# Revit family: LJT-CM
name_source: partatom
category: Lighting Fixtures
revit_build: Autodesk Revit 2013 (Build: 20130531_2115(x64)
units: mm (PartAtom-declared; Revit-internal decimal feet)

## types (8) — shared parameters
Cable Height = 24"
Ceiling Type = Cable Mount
Color Filter = 16777215
Default Elevation = 48"
Description = LED Troffer with Advanced Solid State Technology
Dimming Lamp Color Temperature Shift = Incandescent Lamp Curve
Door = White Flush Steel
Emit Shape Visible in Rendering = No
Finish = Hubbell-Arctic White
Lamp = LED
Load Classification = Lighting
Manufacturer = Columbia Lighting
Manufacturer Fax = 866-898-1065
Model = LJT-CM
Photometric Notes = More IES files download Photometric Web Link
Photometric Web Link = http://www.columbialighting.com
Power Factor = 1
Product Documentation Link = http://cdn.columbialighting.com
Product Page URL = http://www.columbialighting.com
Shielding = Pattern 12 Acrylic Lens
Tilt Angle = 90.00°
URL = http://www.columbialighting.com
Voltage = 120 V

## per-type parameters (varying)
| type | Apparent Load | Color Temp | Emit from Rectangle Length | Emit from Rectangle Width | Glass | Lumen Output | Photometric Web File | Size Option | Wattage Comments | Watts | zz Width 1 |
| LJT24-50XLCM-FSA12-EU | 73 VA | 5000K | 47" | 23" | Hubbell - White Glass | Extra High Lumen | LJT24-50XLG-FSA12-EU.ies | LJT : 24 | 73W | 73 W | 48" |
| LJT24-40XWCM-FSA12-EU | 20 VA | 4000K | 47" | 23" | Hubbell - White Glass | Extra Low Lumen | LJT24-40XWG-FSA12-EU.ies | LJT : 24 | 20W | 20 W | 48" |
| LJT22-50VWCM-FSA12-EU | 13 VA | 5000K | 23" | 23" | Hubbell - White Glass | Very High Lumen | LJT22-50VWG-FSA12-EU.ies | LJT : 22 | 13W | 13 W | 24" |
| LJT14-30MWCM-FSA12-EU | 31 VA | 3000K | 47" | 11" | Hubbell-Arctic White | Medium Low Watts | LJT14-30MWG-FSA12-EU.ies | LJT : 14 | 31W | 31 W | 48" |
| LJT24-35MLG-FSA12-EU | 38 VA | 3500K | 47" | 23" | Hubbell - White Glass | Medium Lumen | LJT24-35MLG-FSA12-EU.ies | LJT : 24 | 34W | 38 W | 48" |
| LJT22-30MLCM-FSA12-EU | 38 VA | 3000K | 23" | 23" | Hubbell - White Glass | Medium Lumen | LJT22-30MLG-FSA12-EU.ies | LJT : 22 | 28W | 38 W | 24" |
| LJT14-35VLCM-FSA12-EU | 59 VA | 3500K | 47" | 11" | Hubbell - White Glass | Very High Lumen | LJT14-35VLG-FSA12-EU.ies | LJT : 14 | 59W | 59 W | 48" |
| LJT14-30HLCM-FSA12-EU | 45 VA | 3000K | 47" | 11" | Hubbell - White Glass | High Lumen | LJT14-30HLG-FSA12-EU.ies | LJT : 14 | 45W | 45 W | 48" |

## geometry (parser evidence)
native form markers: Blend x1, Sweep x3
no freeform markers — native parametric forms only
